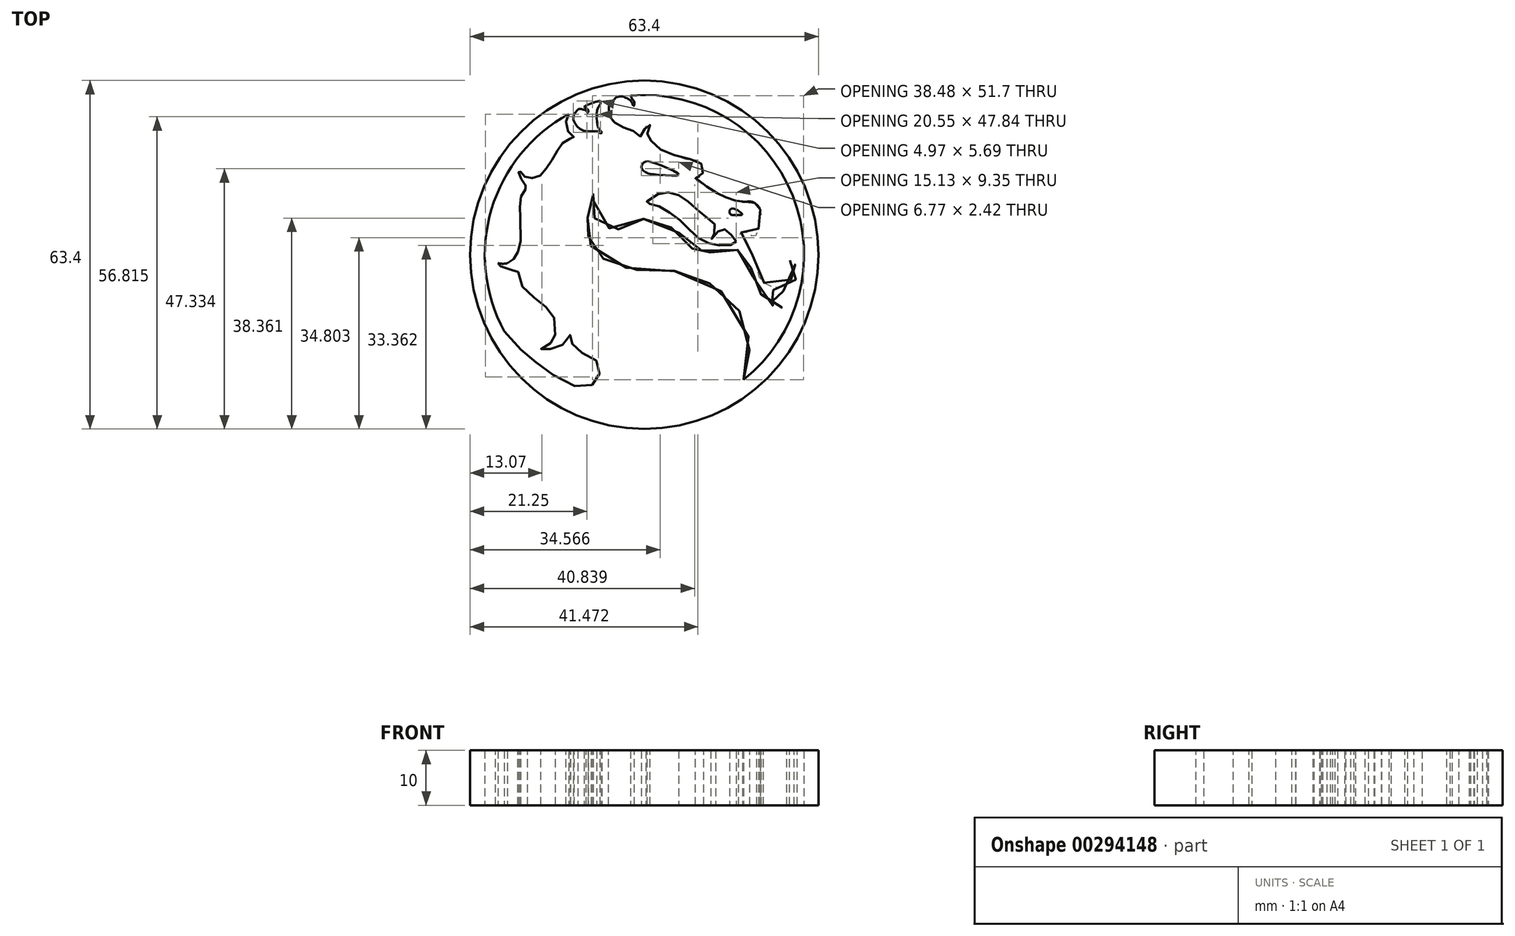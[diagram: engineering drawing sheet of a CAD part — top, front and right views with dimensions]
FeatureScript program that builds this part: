
annotation { "Feature Type Name" : "Feature", "Feature Type Description" : "" }
export const myFeature = defineFeature(function(context is Context, id is Id, definition is map)
    precondition{}
    {
        {
            var Q0;
            Q0=qCreatedBy(makeId("Top.planeOp"),FACE);
            var sketch = newSketch(context, id + "F0", { "sketchPlane" : qUnion([Q0])});
            skCircle(sketch, "E0", {"center": v(0, 0) * mm, "radius": 31.7 * mm});
            skArc(sketch, "E1", {"start": v(-7.96, 27.95) * mm, "mid": v(-9.46, 27.48) * mm, "end": v(-10.93, 26.93) * mm});
            skFitSpline(sketch, "E2", {"points": [v(-25.5, -13.95) * mm, v(-22.7, -17.05) * mm, v(-20.86, -18.67) * mm, v(-18.36, -20.6) * mm, v(-15.95, -22.27) * mm, v(-12.36, -23.98) * mm, v(-10.16, -23.98) * mm, v(-8.94, -23.23) * mm, v(-8.32, -22.18) * mm, v(-8.02, -20.95) * mm, v(-8.32, -19.72) * mm, v(-9.99, -18.54) * mm, v(-11.26, -17.93) * mm, v(-12.22, -17.23) * mm, v(-13.1, -16.26) * mm, v(-13.4, -15.12) * mm, v(-13.4, -14.46) * mm, v(-13.67, -14.9) * mm, v(-14.24, -15.78) * mm, v(-15.03, -16.48) * mm, v(-15.9, -16.96) * mm, v(-17.22, -17.18) * mm, v(-18.06, -17.31) * mm, v(-18.85, -17.31) * mm, v(-18.67, -17.05) * mm, v(-17.88, -16.61) * mm, v(-17.14, -16.13) * mm, v(-16.74, -15.7) * mm, v(-16.52, -15.16) * mm, v(-16.26, -14.6) * mm, v(-16.21, -12.23) * mm, v(-16.54, -11.21) * mm, v(-17.22, -10.16) * mm, v(-18.21, -9.34) * mm, v(-19.41, -8.4) * mm, v(-20.9, -7.06) * mm, v(-22.02, -5.97) * mm, v(-22.84, -4.63) * mm, v(-22.95, -3.05) * mm, v(-22.8, -2.6) * mm, v(-23.37, -2.72) * mm, v(-24.22, -2.82) * mm, v(-25.2, -2.63) * mm, v(-26.25, -2.07) * mm, v(-27.1, -1.5) * mm, v(-27.02, -1.3) * mm, v(-26.62, -1.56) * mm], "startDerivative": vector(73.14, -85.9) * mm, "endDerivative": vector(33.12, -30.6) * mm});
            skArc(sketch, "E3", {"start": v(-26.62, -1.56) * mm, "mid": v(-25.76, -1.65) * mm, "end": v(-24.9, -1.56) * mm});
            skFitSpline(sketch, "E4", {"points": [v(-24.9, -1.56) * mm, v(-24.22, -1.18) * mm, v(-23.58, -0.47) * mm, v(-23.09, 0.44) * mm, v(-22.64, 1.15) * mm, v(-22.61, 7.55) * mm, v(-22.64, 8.78) * mm, v(-22.5, 10.34) * mm, v(-22.04, 11.46) * mm, v(-21.33, 12.17) * mm, v(-21.23, 12.27) * mm, v(-21.7, 12.74) * mm, v(-22.17, 13.42) * mm, v(-22.64, 14.17) * mm, v(-22.87, 14.98) * mm, v(-22.87, 15.55) * mm, v(-22.59, 15.16) * mm, v(-22.12, 14.54) * mm, v(-21.67, 14.15) * mm, v(-20.92, 13.94) * mm, v(-19.85, 14.02) * mm, v(-18.9, 14.46) * mm, v(-18.1, 15.37) * mm, v(-17.27, 16.54) * mm, v(-16.2, 18.27) * mm, v(-15.6, 19.39) * mm, v(-14.82, 20.4) * mm, v(-13.93, 21.03) * mm, v(-12.94, 21.13) * mm, v(-12.76, 21.34) * mm, v(-13.23, 21.6) * mm, v(-13.9, 22.49) * mm, v(-14.24, 24.05) * mm, v(-14, 25.12) * mm, v(-13.7, 25.63) * mm, v(-13.68, 25.64) * mm, v(-13.7, 25.63) * mm], "startDerivative": vector(27.03, 13) * mm, "endDerivative": vector(-4.63, -2.23) * mm});
            skFitSpline(sketch, "E5", {"points": [v(-7.96, 27.95) * mm, v(-7.98, 27.45) * mm, v(-8.51, 26.58) * mm, v(-8.66, 25.66) * mm, v(-8.64, 24.6) * mm, v(-8.59, 23.87) * mm, v(-8.35, 23.06) * mm, v(-8.01, 22.6) * mm, v(-7.74, 22.29) * mm, v(-7.94, 22.07) * mm, v(-8.42, 22.43) * mm, v(-8.9, 22.47) * mm, v(-10.1, 22.45) * mm, v(-11.04, 22.56) * mm, v(-11.98, 23.08) * mm, v(-12.59, 23.82) * mm, v(-12.95, 24.76) * mm, v(-12.72, 25.66) * mm, v(-11.93, 26.5) * mm, v(-11, 26.4) * mm, v(-10.5, 26.12) * mm, v(-10.36, 25.83) * mm, v(-10.19, 26.21) * mm, v(-10.45, 26.55) * mm, v(-10.8, 26.8) * mm, v(-10.93, 26.93) * mm, v(-7.96, 27.95) * mm]});
            skFitSpline(sketch, "E6", {"points": [v(-2.48, 28.95) * mm, v(-2.35, 28.65) * mm, v(-2.13, 28.23) * mm, v(-1.99, 28.1) * mm, v(-1.84, 27.77) * mm, v(-1.9, 27.08) * mm, v(-2.17, 27.53) * mm, v(-2.65, 28.17) * mm, v(-3.07, 28.43) * mm, v(-3.52, 28.61) * mm, v(-3.9, 28.8) * mm, v(-5.2, 28.6) * mm, v(-6, 27.86) * mm, v(-6.43, 27.08) * mm, v(-6.5, 26.48) * mm, v(-6.48, 25.57) * mm, v(-6.28, 25.02) * mm, v(-5.99, 24.56) * mm, v(-5.4, 24.02) * mm, v(-4.7, 23.6) * mm, v(-3.96, 23.23) * mm, v(-3.33, 22.92) * mm, v(-2.48, 22.7) * mm, v(-1.7, 22.35) * mm, v(-1.1, 21.89) * mm, v(-0.75, 21.52) * mm, v(-0.46, 22.2) * mm, v(-0.16, 22.68) * mm, v(0.26, 23.12) * mm, v(0.69, 23.7) * mm, v(1, 23.71) * mm, v(1.02, 23.71) * mm, v(0.96, 23.23) * mm, v(0.72, 22.72) * mm, v(0.56, 21.98) * mm, v(0.72, 21.39) * mm, v(0.94, 21.02) * mm, v(1.38, 20.55) * mm, v(2.37, 19.56) * mm, v(3.61, 18.87) * mm, v(5.26, 18.2) * mm, v(7.33, 17.45) * mm, v(9.38, 17.26) * mm, v(10.03, 16.9) * mm, v(10.74, 15.96) * mm, v(10.78, 15.4) * mm, v(10.53, 14.66) * mm, v(9.97, 14.25) * mm, v(9.57, 14) * mm, v(9.29, 13.82) * mm, v(10.76, 12.74) * mm, v(12.49, 11.67) * mm, v(13.12, 11.27) * mm, v(13.74, 10.96) * mm, v(14.4, 10.7) * mm, v(15.2, 10.29) * mm, v(16.17, 9.97) * mm, v(16.86, 9.8) * mm, v(17.82, 9.66) * mm, v(18.56, 9.64) * mm, v(19.11, 9.7) * mm, v(19.73, 9.59) * mm, v(20.34, 9.22) * mm, v(20.81, 8.74) * mm, v(21.1, 8.24) * mm, v(21.09, 8.23) * mm], "startDerivative": vector(11.35, -25.78) * mm, "endDerivative": vector(-1.39, -4.3) * mm});
            skFitSpline(sketch, "E7", {"points": [v(21.1, 8.23) * mm, v(21.3, 7.6) * mm, v(20.78, 6.66) * mm, v(20.5, 6.47) * mm, v(20.73, 6.03) * mm, v(20.84, 5.17) * mm, v(20.42, 3.7) * mm, v(19.9, 3.18) * mm, v(19.43, 3.6) * mm, v(18.65, 3.98) * mm, v(17.69, 4.04) * mm, v(17.2, 3.96) * mm, v(17.87, 3.36) * mm, v(18.64, 2.35) * mm, v(19.33, 0.75) * mm, v(20, -0.85) * mm, v(20.52, -2.6) * mm, v(21.1, -4.44) * mm, v(22.36, -5.44) * mm, v(23.93, -5.93) * mm, v(25.25, -5.72) * mm, v(26.43, -4.89) * mm, v(27.16, -3.5) * mm, v(27.1, -2.17) * mm, v(26.47, -1.03) * mm, v(27.2, -1.48) * mm, v(27.8, -2.9) * mm, v(27.55, -4.57) * mm, v(26.36, -6.07) * mm, v(24.24, -6.66) * mm, v(21.77, -6.04) * mm, v(22.3, -7.53) * mm, v(24.03, -8.79) * mm, v(25.7, -9.27) * mm, v(25.95, -9.48) * mm, v(24.62, -9.59) * mm, v(22.85, -8.96) * mm, v(21.5, -7.57) * mm, v(20.27, -5.51) * mm, v(19.61, -3.29) * mm, v(18.88, -0.78) * mm, v(17.77, 1.17) * mm, v(16.69, 0.65) * mm, v(14.22, -0.26) * mm, v(11.82, 0.5) * mm, v(10.08, 0.68) * mm, v(9.17, 0.37) * mm, v(8.69, 1.27) * mm, v(6.84, 3.57) * mm, v(4.86, 4.96) * mm, v(2.28, 6.42) * mm, v(0, 6.56) * mm, v(-2.42, 5.7) * mm, v(-4.16, 4.75) * mm, v(-6.28, 4.79) * mm, v(-8.33, 5.8) * mm, v(-9.44, 7.64) * mm, v(-9.44, 10.32) * mm, v(-9.24, 11.02) * mm, v(-9.97, 10.11) * mm, v(-10.56, 8.23) * mm, v(-10.04, 6.21) * mm, v(-9.37, 5.38) * mm, v(-9.86, 4.82) * mm, v(-10.07, 2.63) * mm, v(-9.1, 0.71) * mm, v(-7.29, -0.82) * mm, v(-3.42, -2.35) * mm, v(-0.43, -2.8) * mm, v(4.1, -2.8) * mm, v(8.3, -3.67) * mm, v(12.06, -5.3) * mm, v(15.89, -8.5) * mm, v(18.4, -12.47) * mm, v(19.16, -17.42) * mm, v(18.9, -20.57) * mm, v(18.08, -22.75) * mm, v(18.05, -22.78) * mm], "startDerivative": vector(44.78, -70.7) * mm, "endDerivative": vector(-14.23, -4.64) * mm});
            skPoint(sketch, "E8", {"position": v(-12.1, 26.41) * mm});
            skPoint(sketch, "E9", {"position": v(-11.83, 26.52) * mm});
            skPoint(sketch, "E10", {"position": v(-13.74, 25.58) * mm});
            skFitSpline(sketch, "E11.trimOffspring", {"points": [v(-2.48, 28.95) * mm, v(-2.35, 28.65) * mm, v(-2.13, 28.23) * mm, v(-1.99, 28.1) * mm, v(-1.84, 27.77) * mm, v(-1.9, 27.08) * mm, v(-2.17, 27.53) * mm, v(-2.65, 28.17) * mm, v(-3.07, 28.43) * mm, v(-3.52, 28.61) * mm, v(-3.9, 28.8) * mm, v(-5.2, 28.6) * mm, v(-6, 27.86) * mm, v(-6.43, 27.08) * mm, v(-6.5, 26.48) * mm, v(-6.48, 25.57) * mm, v(-6.28, 25.02) * mm, v(-5.99, 24.56) * mm, v(-5.4, 24.02) * mm, v(-4.7, 23.6) * mm, v(-3.96, 23.23) * mm, v(-3.33, 22.92) * mm, v(-2.48, 22.7) * mm, v(-1.7, 22.35) * mm, v(-1.1, 21.89) * mm, v(-0.75, 21.52) * mm, v(-0.46, 22.2) * mm, v(-0.16, 22.68) * mm, v(0.26, 23.12) * mm, v(0.69, 23.7) * mm, v(1, 23.71) * mm, v(1.02, 23.71) * mm, v(0.96, 23.23) * mm, v(0.72, 22.72) * mm, v(0.56, 21.98) * mm, v(0.72, 21.39) * mm, v(0.94, 21.02) * mm, v(1.38, 20.55) * mm, v(2.37, 19.56) * mm, v(3.61, 18.87) * mm, v(5.26, 18.2) * mm, v(7.33, 17.45) * mm, v(9.38, 17.26) * mm, v(10.03, 16.9) * mm, v(10.74, 15.96) * mm, v(10.78, 15.4) * mm, v(10.53, 14.66) * mm, v(9.97, 14.25) * mm, v(9.57, 14) * mm, v(9.29, 13.82) * mm, v(10.76, 12.74) * mm, v(12.49, 11.67) * mm, v(13.12, 11.27) * mm, v(13.74, 10.96) * mm, v(14.4, 10.7) * mm, v(15.2, 10.29) * mm, v(16.17, 9.97) * mm, v(16.86, 9.8) * mm, v(17.82, 9.66) * mm, v(18.56, 9.64) * mm, v(19.11, 9.7) * mm, v(19.73, 9.59) * mm, v(20.34, 9.22) * mm, v(20.81, 8.74) * mm, v(21.1, 8.24) * mm, v(21.09, 8.23) * mm], "startDerivative": vector(11.35, -25.78) * mm, "endDerivative": vector(-1.39, -4.3) * mm});
            skArc(sketch, "E12.trimOffspring", {"start": v(-3.9, 28.8) * mm, "mid": v(-4.55, 28.7) * mm, "end": v(-5.2, 28.6) * mm});
            skArc(sketch, "E13.trimOffspring", {"start": v(18.08, -22.75) * mm, "mid": v(27, 10.74) * mm, "end": v(-2.48, 28.95) * mm});
            skLineSegment(sketch, "E14", {"start": v(-12.1, 26.41) * mm, "end": v(-11.83, 26.52) * mm});
            skArc(sketch, "E15", {"start": v(-13.74, 25.58) * mm, "mid": v(-27.82, 8.25) * mm, "end": v(-25.5, -13.95) * mm});
            skFitSpline(sketch, "E16", {"points": [v(6.25, 14.54) * mm, v(1.57, 16.78) * mm, v(0, 16.86) * mm, v(-0.56, 15.95) * mm, v(0, 15.19) * mm, v(0.58, 14.82) * mm, v(1.46, 14.68) * mm, v(6.25, 14.54) * mm]});
            skFitSpline(sketch, "E17", {"points": [v(17.84, 7.32) * mm, v(16.29, 8.38) * mm, v(15.53, 8) * mm, v(15.76, 7.32) * mm, v(17.3, 7.25) * mm, v(17.84, 7.32) * mm]});
            skFitSpline(sketch, "E18", {"points": [v(16.7, 2.4) * mm, v(16.25, 1.91) * mm, v(14.28, 1.65) * mm, v(12, 1.99) * mm, v(9.66, 3.16) * mm, v(7.2, 5.58) * mm, v(4.78, 7.55) * mm, v(2.35, 8.95) * mm, v(0.73, 9.25) * mm, v(0.27, 9.4) * mm, v(2.43, 11) * mm, v(4.44, 11.34) * mm, v(6.7, 10.62) * mm, v(9.02, 8.76) * mm, v(11.36, 6.72) * mm, v(12.69, 5.73) * mm, v(12.8, 3.92) * mm, v(12.12, 3) * mm, v(12.5, 2.93) * mm, v(13.9, 4.83) * mm, v(14.92, 4.4) * mm, v(16.06, 3.39) * mm, v(16.7, 2.4) * mm]});
            skSolve(sketch);
        }
        {
            var Q0;
            Q0 = qSketchRegion(id + "F0", true);
            extrude(context, id + "F1", {"entities" : qUnion([Q0]), "depth" : 10 * mm});
        }
    });
